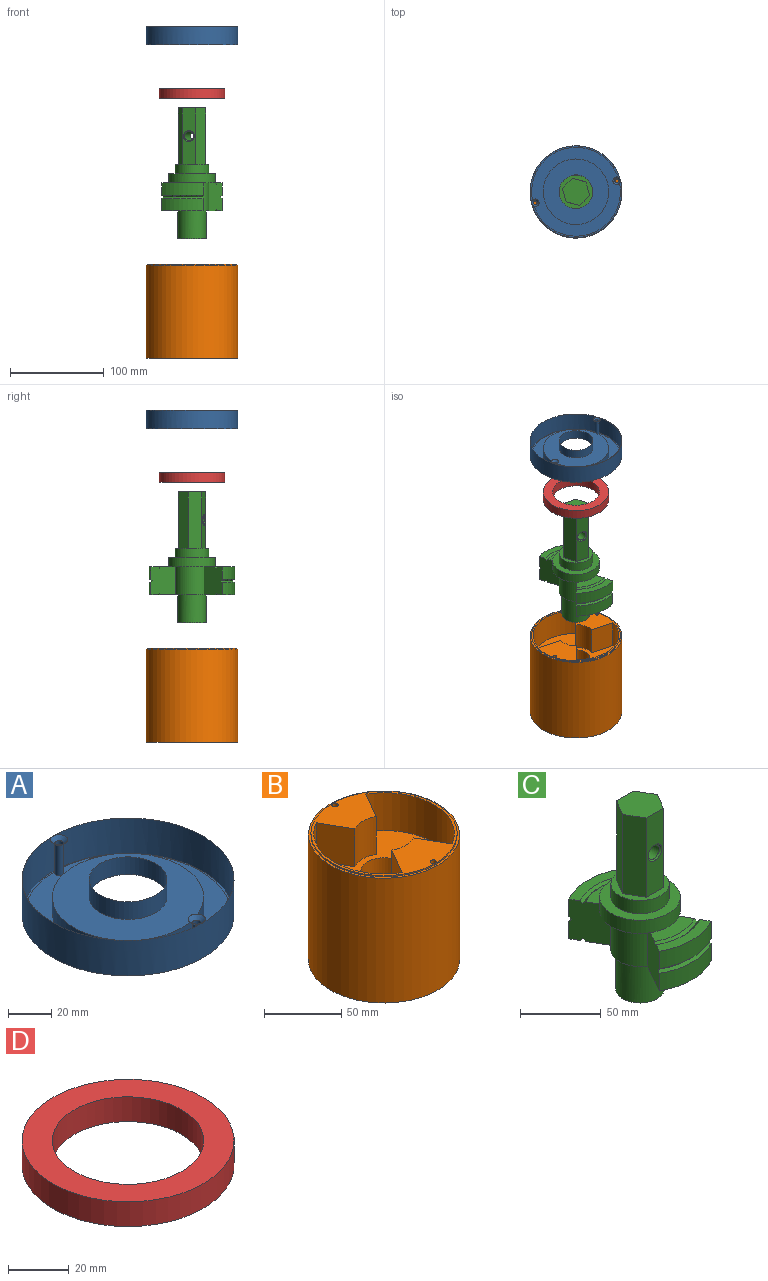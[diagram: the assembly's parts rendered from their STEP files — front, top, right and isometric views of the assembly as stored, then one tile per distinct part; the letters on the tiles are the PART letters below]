
ASSEMBLY  parts=4 mates=5
PART A: 12 faces, bbox 98x98x20 mm
  f0: cylinder r=2mm len=17mm, axis (0,0,-1), area 213.6mm2, adj f6,f10
  f1: cylinder r=49mm len=98mm, axis (0,0,-1), area 6157.5mm2, adj f3,f4
  f2: cylinder r=2mm len=17mm, axis (0,0,-1), area 213.6mm2, adj f6,f11
  f3: plane 98x98mm, normal (0,0,1), area 6424.6mm2, adj f1,f9,f10,f11
  f4: plane 98x98mm, normal (0,0,-1), area 484.6mm2, adj f1,f5
  f5: cylinder r=47.4mm len=94.8mm, axis (0,0,-1), area 297.8mm2, adj f4,f6
  f6: plane 94.8x94.8mm, normal (0,0,-1), area 3184.8mm2, adj f0,f2,f5,f7
  f7: cylinder r=35mm len=70mm, axis (0,0,-1), area 1979.2mm2, adj f6,f8
  f8: plane 70x70mm, normal (0,0,-1), area 2830.6mm2, adj f7,f9
  f9: cylinder r=18mm len=36mm, axis (0,0,-1), area 1131mm2, adj f3,f8
  f10: cone r=2mm half-angle=45deg, axis (0,0,1), area 53.3mm2, adj f0,f3
  f11: cone r=2mm half-angle=45deg, axis (0,0,1), area 53.3mm2, adj f2,f3
PART B: 27 faces, bbox 98x98x100 mm
  f0: cylinder r=49mm len=99mm, axis (0,0,1), area 30479.7mm2, adj f1,f3
  f1: plane 98x98mm, normal (0,0,-1), area 6958.4mm2, adj f0,f20,f21,f22,f23,f24,f25
  f2: cylinder r=47.4mm len=94.8mm, axis (0,0,1), area 297.8mm2, adj f3,f4
  f3: plane 98x98mm, normal (0,0,1), area 484.6mm2, adj f0,f2
  f4: plane 94.8x94.8mm, normal (0,0,1), area 2280.1mm2, adj f2,f5,f6,f7,f8,f9,f10,f11
  f5: plane 30x22.6mm, normal (-0.87,-0.5,0), area 783mm2, adj f4,f6,f12,f13
  f6: cylinder r=45.6mm len=78.98mm, axis (0,0,1), area 2865.1mm2, adj f4,f5,f7,f13
  f7: plane 30x22.6mm, normal (-0.87,0.5,0), area 783mm2, adj f4,f6,f8,f13
  f8: cylinder r=19.5mm len=30mm, axis (0,0,1), area 612.6mm2, adj f4,f7,f9,f13
  f9: plane 30x22.6mm, normal (0.87,0.5,0), area 783mm2, adj f4,f8,f10,f13
  f10: cylinder r=45.6mm len=78.98mm, axis (0,0,1), area 2865.1mm2, adj f4,f9,f11,f13
  f11: plane 30x22.6mm, normal (0.87,-0.5,0), area 783mm2, adj f4,f10,f12,f13
  f12: cylinder r=19.5mm len=30mm, axis (0,0,1), area 612.6mm2, adj f4,f5,f11,f13
  f13: plane 91.2x78.98mm, normal (0,0,1), area 4046.3mm2, adj f5,f6,f7,f8,f9,f10,f11,f12
  f14: cylinder r=15mm len=30mm, axis (0,0,1), area 2827.4mm2, adj f13,f15
  f15: plane 30x30mm, normal (0,0,1), area 706.9mm2, adj f14
  f16: cylinder r=2mm len=10mm, axis (0,0,1), area 125.7mm2, adj f4,f17
  f17: plane 4x4mm, normal (0,0,1), area 12.6mm2, adj f16
  f18: cylinder r=2mm len=10mm, axis (0,0,1), area 125.7mm2, adj f4,f19
  f19: plane 4x4mm, normal (0,0,1), area 12.6mm2, adj f18
  f20: plane 30x15mm, normal (-0.02,1,0), area 450mm2, adj f1,f21,f25,f26
  f21: plane 30x12.87mm, normal (0.86,0.51,0), area 450mm2, adj f1,f20,f22,f26
  f22: plane 30x13.11mm, normal (0.87,-0.49,0), area 450mm2, adj f1,f21,f23,f26
  f23: plane 30x15mm, normal (0.02,-1,0), area 450mm2, adj f1,f22,f24,f26
  f24: plane 30x12.87mm, normal (-0.86,-0.51,0), area 450mm2, adj f1,f23,f25,f26
  f25: plane 30x13.11mm, normal (-0.87,0.49,0), area 450mm2, adj f1,f20,f24,f26
  f26: plane 30x26.22mm, normal (0,0,-1), area 584.6mm2, adj f20,f21,f22,f23,f24,f25
PART C: 47 faces, bbox 50x91x139.7 mm
  f0: plane 36x36mm, normal (0,0,1), area 433.3mm2, adj f36,f37,f38,f39,f40,f41,f42
  f1: cylinder r=15mm len=30mm, axis (0,0,1), area 2799.2mm2, adj f2,f5
  f2: plane 30x30mm, normal (0,0,-1), area 706.9mm2, adj f1
  f3: cylinder r=18mm len=31.18mm, axis (0,0,-1), area 1131mm2, adj f5,f17,f19,f34
  f4: cylinder r=18mm len=31.18mm, axis (0,0,-1), area 1131mm2, adj f5,f18,f20,f35
  f5: plane 69.4x36mm, normal (0,0,-1), area 1232.6mm2, adj f1,f3,f4,f15,f17,f18,f19,f20
  f6: cone r=36.5mm half-angle=45deg, axis (0,0,-1), area 94.9mm2, adj f7,f16,f17,f18
  f7: cone r=38.3mm half-angle=45deg, axis (0,0,1), area 99.7mm2, adj f6,f8,f17,f18
  f8: plane 45.5x12.33mm, normal (0,0,1), area 315.9mm2, adj f7,f9,f17,f18
  f9: cylinder r=45.5mm len=45.5mm, axis (0,0,-1), area 628.9mm2, adj f8,f10,f17,f18
  f10: cone r=45.5mm half-angle=45deg, axis (0,0,1), area 118.9mm2, adj f9,f11,f17,f18
  f11: cone r=43.7mm half-angle=45deg, axis (0,0,-1), area 118.9mm2, adj f10,f12,f17,f18
  f12: cylinder r=45.5mm len=45.5mm, axis (0,0,-1), area 628.9mm2, adj f11,f13,f17,f18
  f13: plane 45.5x12.33mm, normal (0,0,-1), area 315.9mm2, adj f12,f14,f17,f18
  f14: cone r=38.3mm half-angle=45deg, axis (0,0,-1), area 99.7mm2, adj f13,f15,f17,f18
  f15: cone r=36.5mm half-angle=45deg, axis (0,0,1), area 94.9mm2, adj f5,f14,f17,f18
  f16: plane 34.7x13.05mm, normal (0,0,1), area 303.2mm2, adj f6,f17,f18,f32
  f17: plane 30x23.82mm, normal (0.87,0.5,0), area 815.3mm2, adj f3,f5,f6,f7,f8,f9,f10,f11
  f18: plane 30x23.82mm, normal (-0.87,0.5,0), area 815.3mm2, adj f4,f5,f6,f7,f8,f9,f10,f11
  f19: plane 30x23.82mm, normal (0.87,-0.5,0), area 815.3mm2, adj f3,f5,f21,f22,f23,f24,f25,f26
  f20: plane 30x23.82mm, normal (-0.87,-0.5,0), area 815.3mm2, adj f4,f5,f21,f22,f23,f24,f25,f26
  f21: cylinder r=45.5mm len=45.5mm, axis (0,0,-1), area 628.9mm2, adj f19,f20,f22,f27
  f22: plane 45.5x12.33mm, normal (0,0,1), area 315.9mm2, adj f19,f20,f21,f28
  f23: plane 45.5x12.33mm, normal (0,0,-1), area 315.9mm2, adj f19,f20,f24,f30
  f24: cylinder r=45.5mm len=45.5mm, axis (0,0,-1), area 628.9mm2, adj f19,f20,f23,f26
  f25: plane 34.7x13.05mm, normal (0,0,1), area 303.2mm2, adj f19,f20,f29,f32
  f26: cone r=43.7mm half-angle=45deg, axis (0,0,-1), area 118.9mm2, adj f19,f20,f24,f27
  f27: cone r=45.5mm half-angle=45deg, axis (0,0,1), area 118.9mm2, adj f19,f20,f21,f26
  f28: cone r=38.3mm half-angle=45deg, axis (0,0,1), area 99.7mm2, adj f19,f20,f22,f29
  f29: cone r=36.5mm half-angle=45deg, axis (0,0,-1), area 94.9mm2, adj f19,f20,f25,f28
  f30: cone r=38.3mm half-angle=45deg, axis (0,0,-1), area 99.7mm2, adj f19,f20,f23,f31
  f31: cone r=36.5mm half-angle=45deg, axis (0,0,1), area 94.9mm2, adj f5,f19,f20,f30
  f32: cylinder r=25mm len=50mm, axis (0,0,-1), area 1570.8mm2, adj f16,f25,f33,f34,f35
  f33: plane 50x50mm, normal (0,0,1), area 945.6mm2, adj f32,f36
  f34: plane 43.3x16mm, normal (0,0,-1), area 315.2mm2, adj f3,f17,f19,f32
  f35: plane 43.3x16mm, normal (0,0,-1), area 315.2mm2, adj f4,f18,f20,f32
  f36: cylinder r=18mm len=36mm, axis (0,0,-1), area 1131mm2, adj f0,f33
  f37: plane 60x15mm, normal (0,-1,0), area 786.9mm2, adj f0,f38,f42,f43,f45
  f38: plane 60x12.99mm, normal (0.87,-0.5,0), area 900mm2, adj f0,f37,f39,f43
  f39: plane 60x12.99mm, normal (0.87,0.5,0), area 900mm2, adj f0,f38,f40,f43
  f40: plane 60x15mm, normal (0,1,0), area 786.9mm2, adj f0,f39,f41,f43,f46
  f41: plane 60x12.99mm, normal (-0.87,0.5,0), area 900mm2, adj f0,f40,f42,f43
  f42: plane 60x12.99mm, normal (-0.87,-0.5,0), area 900mm2, adj f0,f37,f41,f43
  f43: plane 30x25.98mm, normal (0,0,1), area 584.6mm2, adj f37,f38,f39,f40,f41,f42
  f44: cylinder r=5mm len=23.98mm, axis (0,-1,0), area 753.4mm2, adj f45,f46
  f45: cone r=5mm half-angle=45deg, axis (0,-1,0), area 48.9mm2, adj f37,f44
  f46: cone r=6mm half-angle=45deg, axis (0,1,0), area 48.9mm2, adj f40,f44
PART D: 4 faces, bbox 70x70x10 mm
  f0: cylinder r=25mm len=50mm, axis (0,0,-1), area 1570.8mm2, adj f2,f3
  f1: cylinder r=35mm len=70mm, axis (0,0,-1), area 2199.1mm2, adj f2,f3
  f2: plane 70x70mm, normal (0,0,1), area 1885mm2, adj f0,f1
  f3: plane 70x70mm, normal (0,0,-1), area 1885mm2, adj f0,f1
PLACE A rot(axis=(0,0,1),105.2deg) t=(18.21,8.12,234.55)mm
PLACE B rot(axis=(0,0,-1),74.8deg) t=(18.21,8.12,0)mm fixed
PLACE C rot(axis=(0,0,-1),14.8deg) t=(18.21,8.12,57)mm
PLACE D rot(axis=(0,0,1),15.2deg) t=(18.21,8.12,177.55)mm
MATE parallel A.f1 <-> B.f0  axis (0,0,-1) through (18.21,8.12,234.55)mm
MATE cylindrical A.f2 <-> B.f18  axis (0,0,1) through (61.64,19.88,252.55)mm
MATE cylindrical C.f1 <-> B.f14  axis (0,0,-1) through (18.21,8.12,27.3)mm
MATE slider D.f0 <-> A.f9  axis (0,0,1) through (18.21,8.12,187.55)mm
MATE cylindrical A.f0 <-> B.f16  axis (0,0,1) through (-25.23,-3.65,254.55)mm
